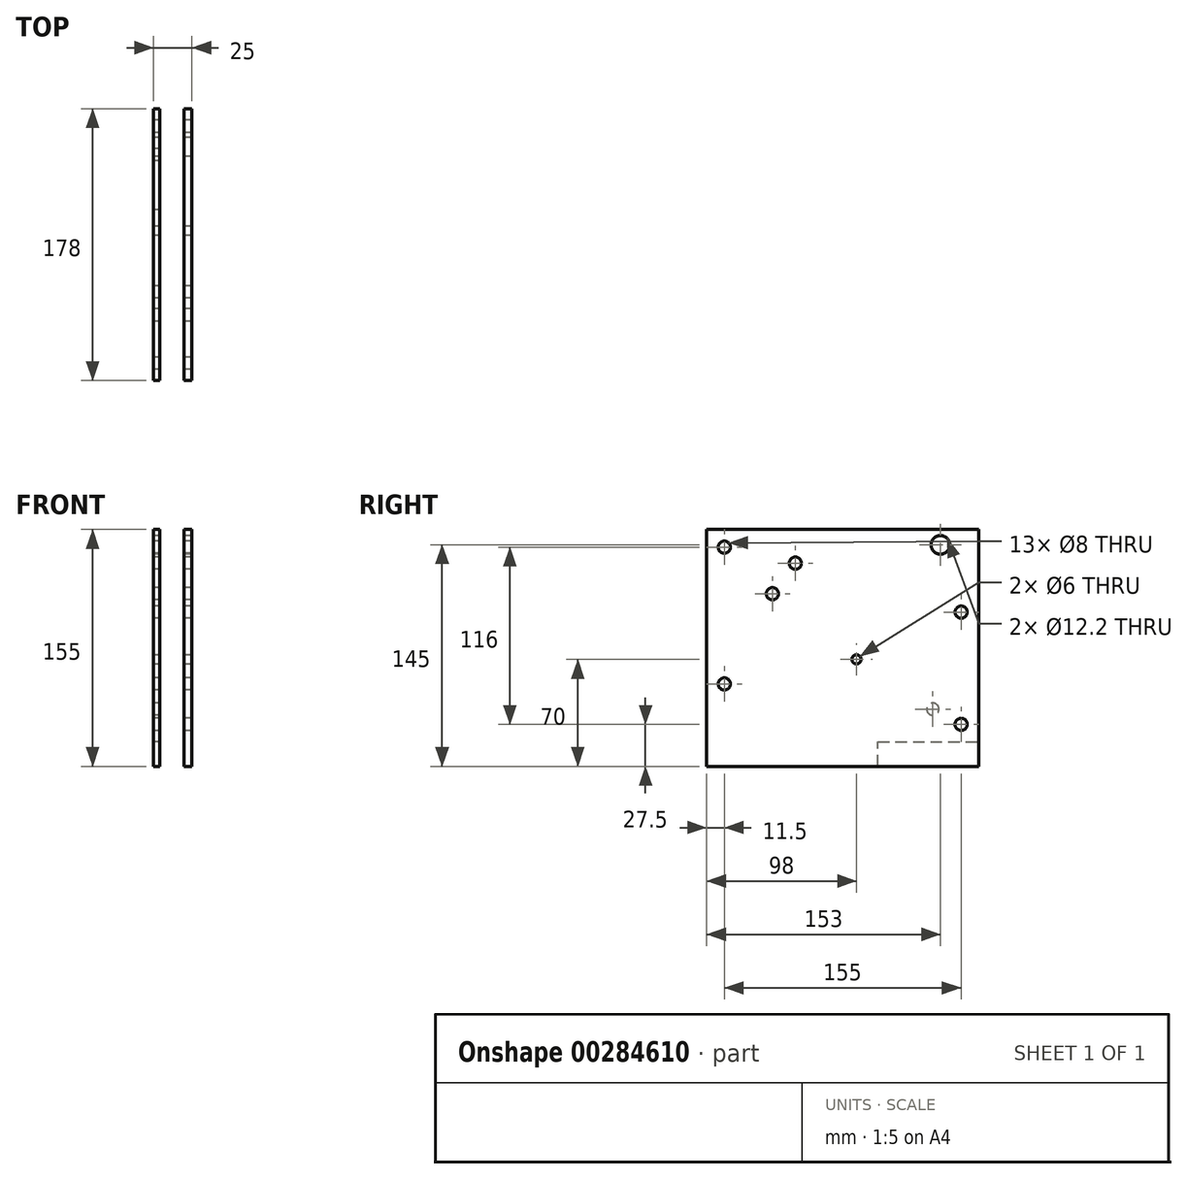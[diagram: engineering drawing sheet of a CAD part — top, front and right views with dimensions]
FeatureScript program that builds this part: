
annotation { "Feature Type Name" : "Feature", "Feature Type Description" : "" }
export const myFeature = defineFeature(function(context is Context, id is Id, definition is map)
    precondition{}
    {
        {
            var Q0;
            Q0=qCreatedBy(makeId("Right.planeOp"),FACE);
            var sketch = newSketch(context, id + "F0", { "sketchPlane" : qUnion([Q0])});
            skLineSegment(sketch, "E0.bottom", {"start": v(0, 0) * mm, "end": v(84, 0) * mm});
            skLineSegment(sketch, "E0.top", {"start": v(0, 155) * mm, "end": v(150, 155) * mm});
            skLineSegment(sketch, "E0.left", {"start": v(0, 0) * mm, "end": v(0, 155) * mm, "construction": true});
            skLineSegment(sketch, "E0.right", {"start": v(150, 16) * mm, "end": v(150, 155) * mm, "construction": true});
            skPoint(sketch, "E1", {"position": v(70, 70) * mm});
            skCircle(sketch, "E2", {"center": v(70, 70) * mm, "radius": 3 * mm});
            skCircle(sketch, "E3", {"center": v(30, 133) * mm, "radius": 4 * mm});
            skCircle(sketch, "E4", {"center": v(15, 113) * mm, "radius": 4 * mm});
            skCircle(sketch, "E5", {"center": v(125, 145) * mm, "radius": 6.1 * mm});
            skLineSegment(sketch, "E6", {"start": v(84, 0) * mm, "end": v(84, 16) * mm});
            skLineSegment(sketch, "E7", {"start": v(84, 16) * mm, "end": v(150, 16) * mm});
            skLineSegment(sketch, "E8", {"start": v(0, 155) * mm, "end": v(-28, 155) * mm});
            skLineSegment(sketch, "E9", {"start": v(-28, 155) * mm, "end": v(-28, 0) * mm});
            skLineSegment(sketch, "E10", {"start": v(-28, 0) * mm, "end": v(0, 0) * mm});
            skCircle(sketch, "E11", {"center": v(-16.5, 143.5) * mm, "radius": 4 * mm});
            skCircle(sketch, "E12", {"center": v(-16.5, 54) * mm, "radius": 4 * mm});
            skLineSegment(sketch, "E13", {"start": v(150, 155) * mm, "end": v(150, 155) * mm});
            skLineSegment(sketch, "E14", {"start": v(150, 155) * mm, "end": v(150, 16) * mm});
            skLineSegment(sketch, "E15", {"start": v(150, 16) * mm, "end": v(150, 16) * mm});
            skCircle(sketch, "E16", {"center": v(138.5, 101) * mm, "radius": 4 * mm});
            skCircle(sketch, "E17", {"center": v(138.5, 27.5) * mm, "radius": 4 * mm});
            skCircle(sketch, "E18", {"center": v(20, 37.5) * mm, "radius": 4 * mm, "construction": true});
            skCircle(sketch, "E19", {"center": v(120, 37.5) * mm, "radius": 4 * mm});
            skSolve(sketch);
        }
        {
            var Q0;
            Q0=qSketchRegion(id+"F0",true);
            extrude(context, id + "F1", {"entities" : qUnion([Q0]), "depth" : 4 * mm});
        }
        {
            var Q0;
            Q0=qCreatedBy(makeId("Right.planeOp"),FACE);
            var sketch = newSketch(context, id + "F2", { "sketchPlane" : qUnion([Q0])});
            skLineSegment(sketch, "E20.bottom", {"start": v(0, 0) * mm, "end": v(150, 0) * mm});
            skLineSegment(sketch, "E20.top", {"start": v(0, 155) * mm, "end": v(150, 155) * mm});
            skLineSegment(sketch, "E20.left", {"start": v(0, 0) * mm, "end": v(0, 155) * mm, "construction": true});
            skLineSegment(sketch, "E20.right", {"start": v(150, 0) * mm, "end": v(150, 155) * mm, "construction": true});
            skCircle(sketch, "E21", {"center": v(70, 70) * mm, "radius": 3 * mm});
            skCircle(sketch, "E22", {"center": v(30, 133) * mm, "radius": 4 * mm});
            skCircle(sketch, "E23", {"center": v(15, 113) * mm, "radius": 4 * mm});
            skCircle(sketch, "E24", {"center": v(125, 145) * mm, "radius": 6.1 * mm});
            skLineSegment(sketch, "E25", {"start": v(0, 155) * mm, "end": v(-28, 155) * mm});
            skLineSegment(sketch, "E26", {"start": v(-28, 155) * mm, "end": v(-28, 0) * mm});
            skLineSegment(sketch, "E27", {"start": v(-28, 0) * mm, "end": v(0, 0) * mm});
            skLineSegment(sketch, "E28", {"start": v(150, 155) * mm, "end": v(150, 155) * mm});
            skLineSegment(sketch, "E29", {"start": v(150, 155) * mm, "end": v(150, 0) * mm});
            skLineSegment(sketch, "E30", {"start": v(150, 0) * mm, "end": v(150, 0) * mm});
            skCircle(sketch, "E31", {"center": v(-16.5, 143.5) * mm, "radius": 4 * mm});
            skCircle(sketch, "E32", {"center": v(-16.5, 54) * mm, "radius": 4 * mm});
            skCircle(sketch, "E33", {"center": v(138.5, 101) * mm, "radius": 4 * mm});
            skCircle(sketch, "E34", {"center": v(138.5, 27.5) * mm, "radius": 4 * mm});
            skSolve(sketch);
        }
        {
            var Q0;
            Q0=qSketchRegion(id+"F2",true);
            extrude(context, id + "F3", {"entities" : qUnion([Q0]), "depth" : 5 * mm});
        }
        {
            var Q0;
            Q0=makeQuery(id+"F3.opExtrude","SWEPT_BODY",BODY,{"disambiguationData":[OSD([sQuery(id+"F2.wireOp",EDGE,"E20.bottom"),sQuery(id+"F2.wireOp",EDGE,"E20.top"),sQuery(id+"F2.wireOp",EDGE,"E20.left"),sQuery(id+"F2.wireOp",EDGE,"E20.right"),sQuery(id+"F2.wireOp",EDGE,"E21"),sQuery(id+"F2.wireOp",EDGE,"E22"),sQuery(id+"F2.wireOp",EDGE,"E23"),sQuery(id+"F2.wireOp",EDGE,"E24")])]});
            transform(context, id + "F4", {"entities" : qUnion([Q0]), "transformType" : TransformType.TRANSLATION_3D, "dx" : 20 * mm, "dy" : 0 * mm, "dz" : 0 * mm, "makeCopy" : false});
        }
    });
